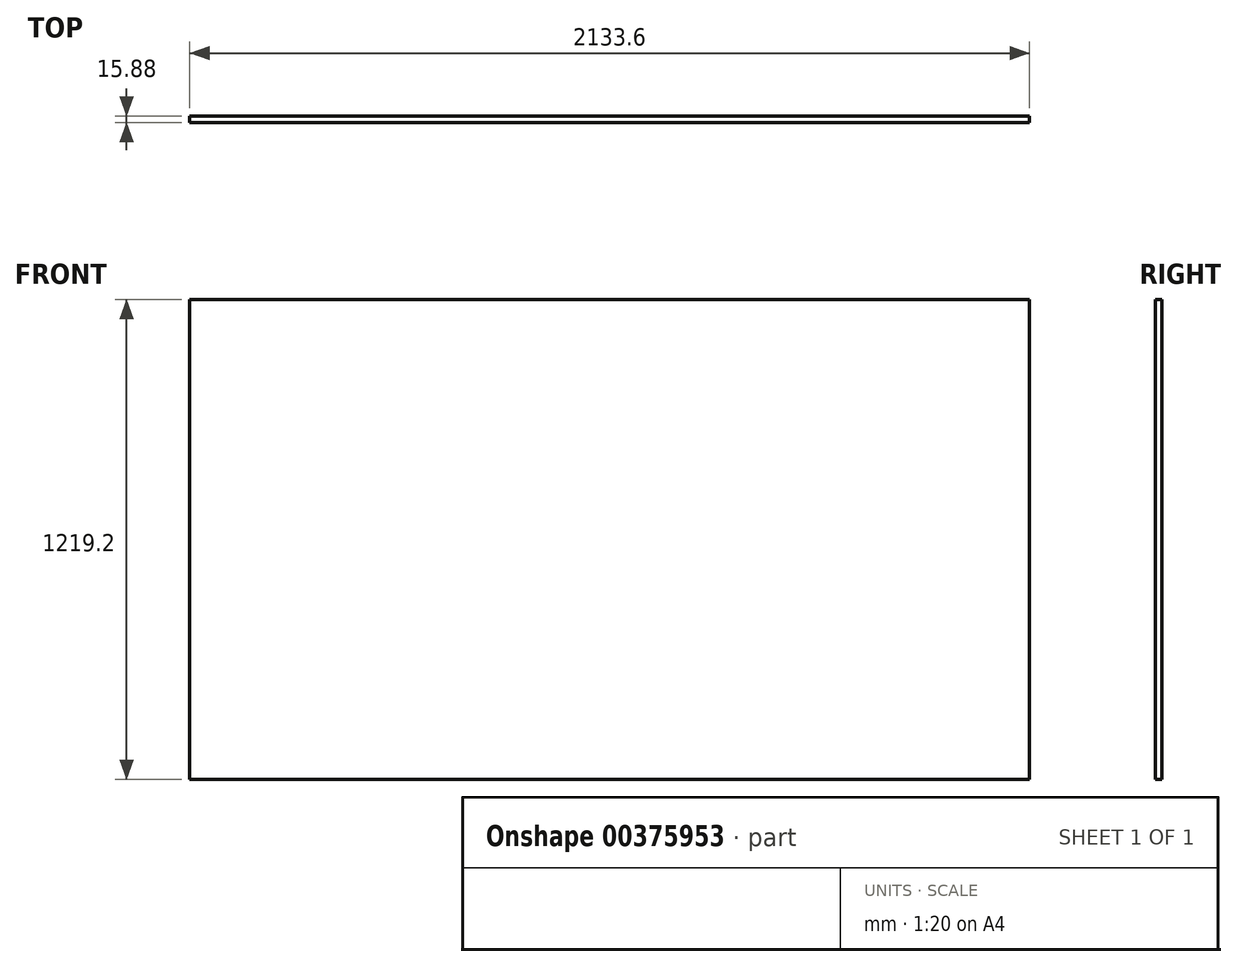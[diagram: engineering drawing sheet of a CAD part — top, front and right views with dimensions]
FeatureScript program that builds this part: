
annotation { "Feature Type Name" : "Feature", "Feature Type Description" : "" }
export const myFeature = defineFeature(function(context is Context, id is Id, definition is map)
    precondition{}
    {
        {
            var Q0;
            Q0=qCreatedBy(makeId("Front.planeOp"),FACE);
            var sketch = newSketch(context, id + "F0", { "sketchPlane" : qUnion([Q0])});
            skLineSegment(sketch, "E0.bottom", {"start": v(1066.8, -609.6) * mm, "end": v(-1066.8, -609.6) * mm});
            skLineSegment(sketch, "E0.top", {"start": v(1066.8, 609.6) * mm, "end": v(-1066.8, 609.6) * mm});
            skLineSegment(sketch, "E0.left", {"start": v(1066.8, -609.6) * mm, "end": v(1066.8, 609.6) * mm});
            skLineSegment(sketch, "E0.right", {"start": v(-1066.8, -609.6) * mm, "end": v(-1066.8, 609.6) * mm});
            skPoint(sketch, "E0.middle", {"position": v(0, 0) * mm});
            skSolve(sketch);
        }
        {
            var Q0;
            Q0=qSketchRegion(id+"F0",true);
            extrude(context, id + "F1", {"entities" : qUnion([Q0]), "depth" : 15.88 * mm});
        }
    });
